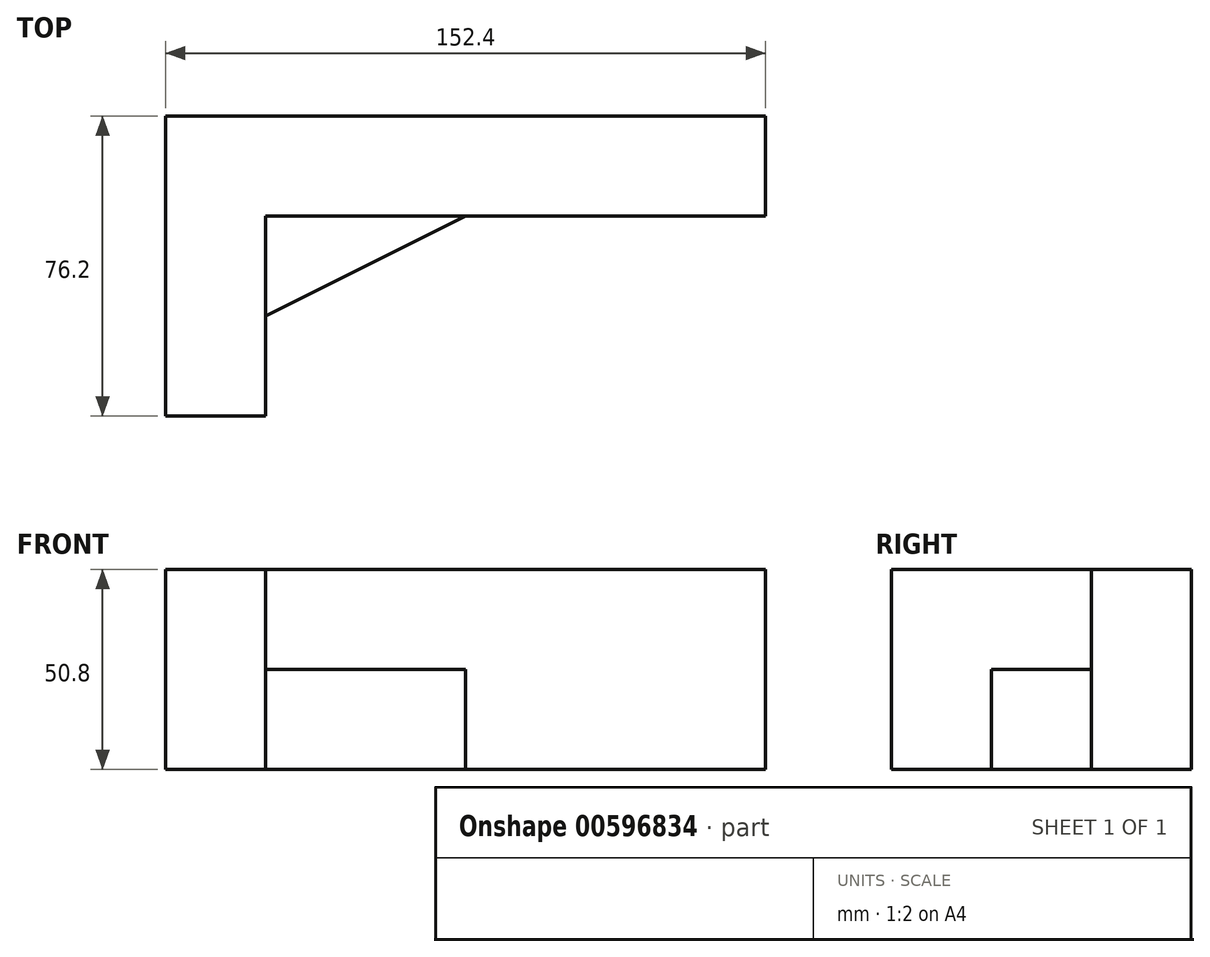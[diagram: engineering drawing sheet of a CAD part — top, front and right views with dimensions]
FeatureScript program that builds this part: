
annotation { "Feature Type Name" : "Feature", "Feature Type Description" : "" }
export const myFeature = defineFeature(function(context is Context, id is Id, definition is map)
    precondition{}
    {
        {
            var Q0;
            Q0=qCreatedBy(makeId("Top.planeOp"),FACE);
            var sketch = newSketch(context, id + "F0", { "sketchPlane" : qUnion([Q0])});
            skLineSegment(sketch, "E0", {"start": v(0, 0) * mm, "end": v(0, 76.2) * mm});
            skLineSegment(sketch, "E1", {"start": v(0, 76.2) * mm, "end": v(152.4, 76.2) * mm});
            skLineSegment(sketch, "E2", {"start": v(152.4, 76.2) * mm, "end": v(152.4, 50.8) * mm});
            skLineSegment(sketch, "E3", {"start": v(152.4, 50.8) * mm, "end": v(25.4, 50.8) * mm});
            skLineSegment(sketch, "E4", {"start": v(25.4, 50.8) * mm, "end": v(25.4, 0) * mm});
            skLineSegment(sketch, "E5", {"start": v(25.4, 0) * mm, "end": v(0, 0) * mm});
            skSolve(sketch);
        }
        {
            var Q0;
            Q0=makeQuery(id+"F0.imprint","IMPRINT",FACE,{"disambiguationData":[TD([[makeQuery(id+"F0.imprint","IMPRINT",EDGE,{"derivedFrom":sQuery(id+"F0.wireOp",EDGE,"E0")}),-1.0]])]});
            extrude(context, id + "F1", {"entities" : qUnion([Q0]), "depth" : 50.8 * mm, "offsetDistance" : 25.4 * mm});
        }
        {
            var Q0;
            Q0=makeQuery(id+"F1.opExtrude","CAP_FACE",FACE,{"disambiguationData":[OSD([sQuery(id+"F0.wireOp",EDGE,"E0"),sQuery(id+"F0.wireOp",EDGE,"E1"),sQuery(id+"F0.wireOp",EDGE,"E2"),sQuery(id+"F0.wireOp",EDGE,"E3"),sQuery(id+"F0.wireOp",EDGE,"E4"),sQuery(id+"F0.wireOp",EDGE,"E5")])],"isStart":true});
            var sketch = newSketch(context, id + "F2", { "sketchPlane" : qUnion([Q0])});
            skLineSegment(sketch, "E6", {"start": v(25.4, -50.8) * mm, "end": v(25.4, -25.4) * mm});
            skLineSegment(sketch, "E7", {"start": v(25.4, -50.8) * mm, "end": v(76.2, -50.8) * mm});
            skLineSegment(sketch, "E8", {"start": v(25.4, -25.4) * mm, "end": v(76.2, -50.8) * mm});
            skSolve(sketch);
        }
        {
            var Q0;
            Q0 = qSketchRegion(id + "F2", true);
            extrude(context, id + "F3", {"entities" : qUnion([Q0]), "operationType" : NewBodyOperationType.ADD, "oppositeDirection" : true, "depth" : 25.4 * mm, "offsetDistance" : 25.4 * mm});
        }
    });
